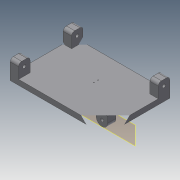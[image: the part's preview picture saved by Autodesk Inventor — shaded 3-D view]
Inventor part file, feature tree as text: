
AUTODESK INVENTOR PART (.ipt)
format: ipt  version: 2014 SP1 (Build 180222100, 222)  size: 184,320 bytes
history: native  units: in
note: dims shown in document units (in); Inventor stores cm internally (conversion verified against a paired STEP export)
features: extrude x5, sketch x5, pattern_linear x3, reference x3, plane x2, fillet x1
ambient origin geometry x8: Origin, YZ Plane, XZ Plane, XY Plane, X Axis, Y Axis, Z Axis, Center Point
bodies: Solid1 (feature_tree)
feature tree (19):
  plane  "Work Plane1"
  extrude  "Extrusion1"  Depth=0.315in TaperAngle=0.0deg
  pattern_linear  "Rectangular Pattern2"  Count1=2 Spacing1=2.0079in
  extrude  "Extrusion3"  Depth=0.1969in
  plane  "Work Plane2"
  extrude  "Extrusion4"  Depth=2.4409in
  pattern_linear  "Rectangular Pattern3"  Spacing1=0.5906in  [1 undecoded]
  extrude  "Extrusion5"  Depth=0.7874in
  extrude  "Extrusion6"  Depth=0.4331in
  fillet  "Fillet1"  Radius=0.315in
  pattern_linear  "Rectangular Pattern4"  Spacing1=0.5315in  [1 undecoded]
  sketch  "Sketch1"  dims[d0=0.4331in d2=0.315in d3=0.0in]
  reference  "Reference1"
  reference  "Reference2"
  sketch  "Sketch3"  dims[d4=0.4232in d14=0.7874in d16=2.0079in d17=0.7874in d19=0.7874in]
  sketch  "Sketch4"  dims[d20=0.1969in d21=0.0in d29=1.8012in]
  reference  "Reference3"
  sketch  "Sketch5"  dims[d30=1.8012in d31=2.4409in]
  sketch  "Sketch6"  dims[d32=0.0295in d33=0.5906in d34=0.0in d35=0.7874in d37=0.1575in d38=0.4331in d39=0.315in d40=0.5315in d41=0.0in d42=0.1181in d43=0.2165in d44=0.2165in d45=0.9685in d46=0.0in d47=0.1181in d48=0.7874in d50=2.0079in d51=0.7874in d53=3.2874in]
note: 2 required parameter values undecoded (feature->parameter linkage not recoverable at this tier; creation-order binding heuristic only, values carry confidence <= 0.55)
